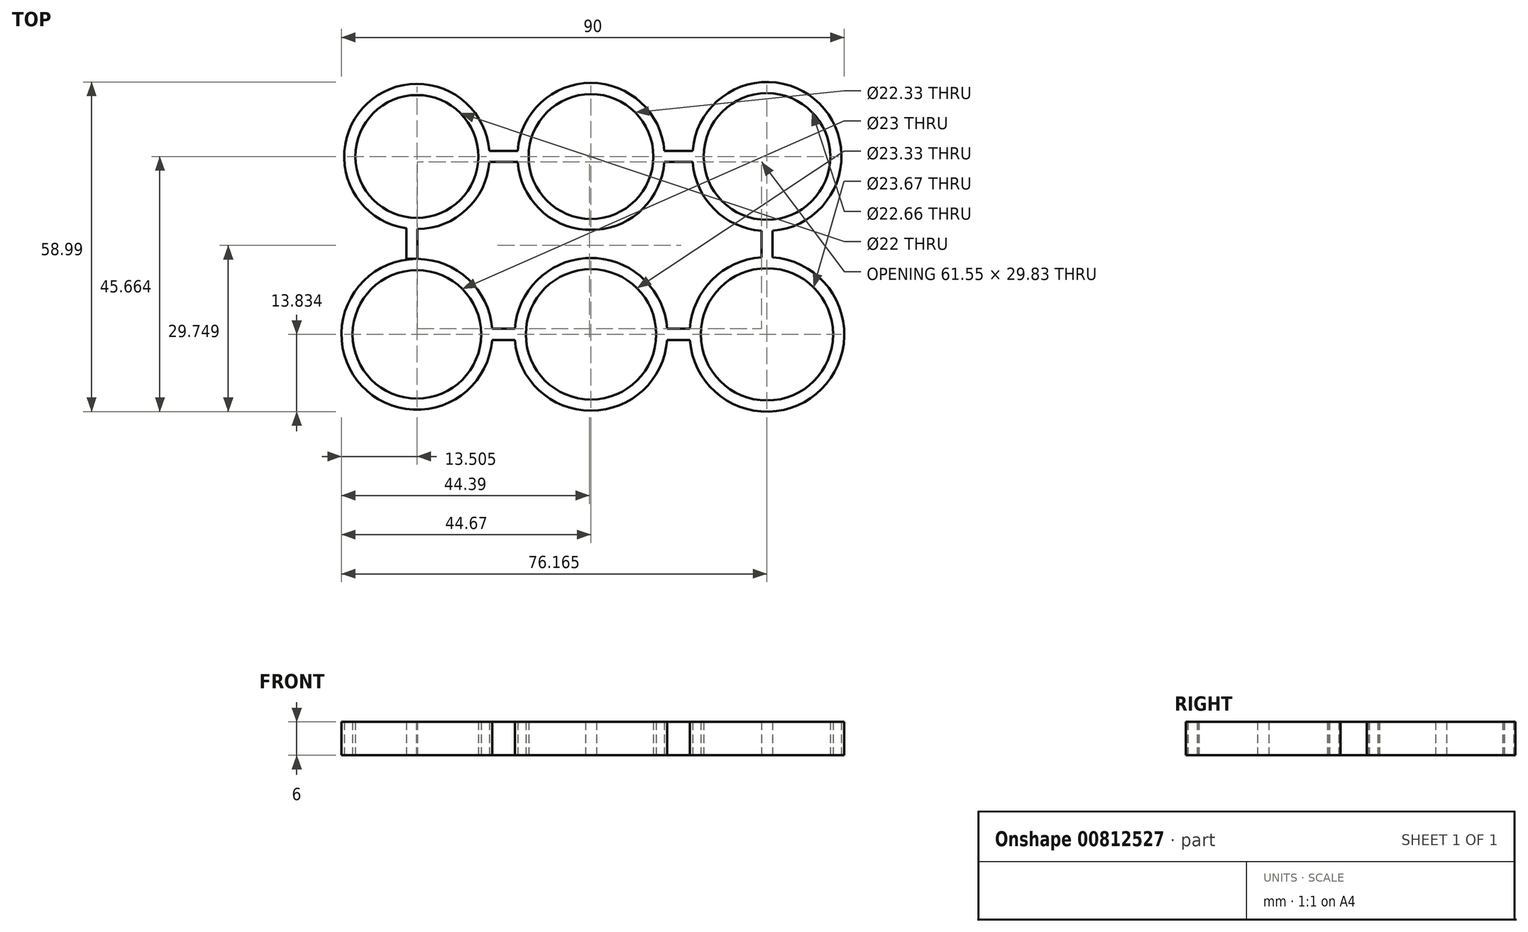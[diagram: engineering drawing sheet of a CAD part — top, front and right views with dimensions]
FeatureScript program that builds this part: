
annotation { "Feature Type Name" : "Feature", "Feature Type Description" : "" }
export const myFeature = defineFeature(function(context is Context, id is Id, definition is map)
    precondition{}
    {
        {
            var Q0;
            Q0=qCreatedBy(makeId("Top.planeOp"),FACE);
            var sketch = newSketch(context, id + "F0", { "sketchPlane" : qUnion([Q0])});
            skCircle(sketch, "E0", {"center": v(-31.16, 15.66) * mm, "radius": 11 * mm});
            skCircle(sketch, "E1", {"center": v(0, 15.66) * mm, "radius": 11.16 * mm});
            skCircle(sketch, "E2", {"center": v(31.5, 15.66) * mm, "radius": 11.33 * mm});
            skCircle(sketch, "E3", {"center": v(-31.16, -16.17) * mm, "radius": 11.5 * mm});
            skCircle(sketch, "E4", {"center": v(0, -16.17) * mm, "radius": 11.66 * mm});
            skCircle(sketch, "E5", {"center": v(31.5, -16.17) * mm, "radius": 11.84 * mm});
            skCircle(sketch, "E6.0", {"center": v(-31.16, 15.66) * mm, "radius": 13 * mm});
            skCircle(sketch, "E7.0", {"center": v(0, 15.66) * mm, "radius": 13.16 * mm});
            skCircle(sketch, "E8.0", {"center": v(31.5, 15.66) * mm, "radius": 13.33 * mm});
            skCircle(sketch, "E9.0", {"center": v(-31.16, -16.17) * mm, "radius": 13.5 * mm});
            skCircle(sketch, "E10.0", {"center": v(0, -16.17) * mm, "radius": 13.67 * mm});
            skCircle(sketch, "E11.0", {"center": v(31.5, -16.17) * mm, "radius": 13.84 * mm});
            skLineSegment(sketch, "E12.bottom", {"start": v(1, -2.54) * mm, "end": v(-1, -2.54) * mm});
            skLineSegment(sketch, "E12.top", {"start": v(1, 2.54) * mm, "end": v(-1, 2.54) * mm});
            skLineSegment(sketch, "E12.left", {"start": v(1, -2.54) * mm, "end": v(1, 2.54) * mm});
            skLineSegment(sketch, "E12.right", {"start": v(-1, -2.54) * mm, "end": v(-1, 2.54) * mm});
            skPoint(sketch, "E12.middle", {"position": v(0, 0) * mm});
            skLineSegment(sketch, "E13.bottom", {"start": v(32.5, -2.37) * mm, "end": v(30.5, -2.37) * mm});
            skLineSegment(sketch, "E13.top", {"start": v(32.5, 2.37) * mm, "end": v(30.5, 2.37) * mm});
            skLineSegment(sketch, "E13.left", {"start": v(32.5, -2.37) * mm, "end": v(32.5, 2.37) * mm});
            skLineSegment(sketch, "E13.right", {"start": v(30.5, -2.37) * mm, "end": v(30.5, 2.37) * mm});
            skPoint(sketch, "E13.middle", {"position": v(31.5, 0) * mm});
            skLineSegment(sketch, "E14.bottom", {"start": v(-31.06, -2.67) * mm, "end": v(-33.06, -2.67) * mm});
            skLineSegment(sketch, "E14.top", {"start": v(-31.06, 2.8) * mm, "end": v(-33.06, 2.8) * mm});
            skLineSegment(sketch, "E14.left", {"start": v(-31.06, -2.67) * mm, "end": v(-31.06, 2.8) * mm});
            skLineSegment(sketch, "E14.right", {"start": v(-33.06, -2.67) * mm, "end": v(-33.06, 2.8) * mm});
            skPoint(sketch, "E14.middle", {"position": v(-32.06, 0.07) * mm});
            skLineSegment(sketch, "E15.bottom", {"start": v(-13.63, -17.17) * mm, "end": v(-17.7, -17.17) * mm});
            skLineSegment(sketch, "E15.top", {"start": v(-13.63, -15.17) * mm, "end": v(-17.7, -15.17) * mm});
            skLineSegment(sketch, "E15.left", {"start": v(-13.63, -17.17) * mm, "end": v(-13.63, -15.17) * mm});
            skLineSegment(sketch, "E15.right", {"start": v(-17.7, -17.17) * mm, "end": v(-17.7, -15.17) * mm});
            skPoint(sketch, "E15.middle", {"position": v(-15.67, -16.17) * mm});
            skLineSegment(sketch, "E16.bottom", {"start": v(17.7, -17.17) * mm, "end": v(13.63, -17.17) * mm});
            skLineSegment(sketch, "E16.top", {"start": v(17.7, -15.17) * mm, "end": v(13.63, -15.17) * mm});
            skLineSegment(sketch, "E16.left", {"start": v(17.7, -17.17) * mm, "end": v(17.7, -15.17) * mm});
            skLineSegment(sketch, "E16.right", {"start": v(13.63, -17.17) * mm, "end": v(13.63, -15.17) * mm});
            skPoint(sketch, "E16.middle", {"position": v(15.66, -16.17) * mm});
            skLineSegment(sketch, "E17.bottom", {"start": v(-13.13, 14.66) * mm, "end": v(-18.2, 14.66) * mm});
            skLineSegment(sketch, "E17.top", {"start": v(-13.13, 16.66) * mm, "end": v(-18.2, 16.66) * mm});
            skLineSegment(sketch, "E17.left", {"start": v(-13.13, 14.66) * mm, "end": v(-13.13, 16.66) * mm});
            skLineSegment(sketch, "E17.right", {"start": v(-18.2, 14.66) * mm, "end": v(-18.2, 16.66) * mm});
            skPoint(sketch, "E17.middle", {"position": v(-15.67, 15.66) * mm});
            skLineSegment(sketch, "E18.bottom", {"start": v(18.2, 14.66) * mm, "end": v(13.13, 14.66) * mm});
            skLineSegment(sketch, "E18.top", {"start": v(18.2, 16.66) * mm, "end": v(13.13, 16.66) * mm});
            skLineSegment(sketch, "E18.left", {"start": v(18.2, 14.66) * mm, "end": v(18.2, 16.66) * mm});
            skLineSegment(sketch, "E18.right", {"start": v(13.13, 14.66) * mm, "end": v(13.13, 16.66) * mm});
            skPoint(sketch, "E18.middle", {"position": v(15.66, 15.66) * mm});
            skSolve(sketch);
        }
        {
            var Q0;
            Q0 = qSketchRegion(id + "F0", true);
            extrude(context, id + "F1", {"entities" : qUnion([Q0]), "depth" : 6 * mm, "offsetDistance" : 25 * mm});
        }
    });
